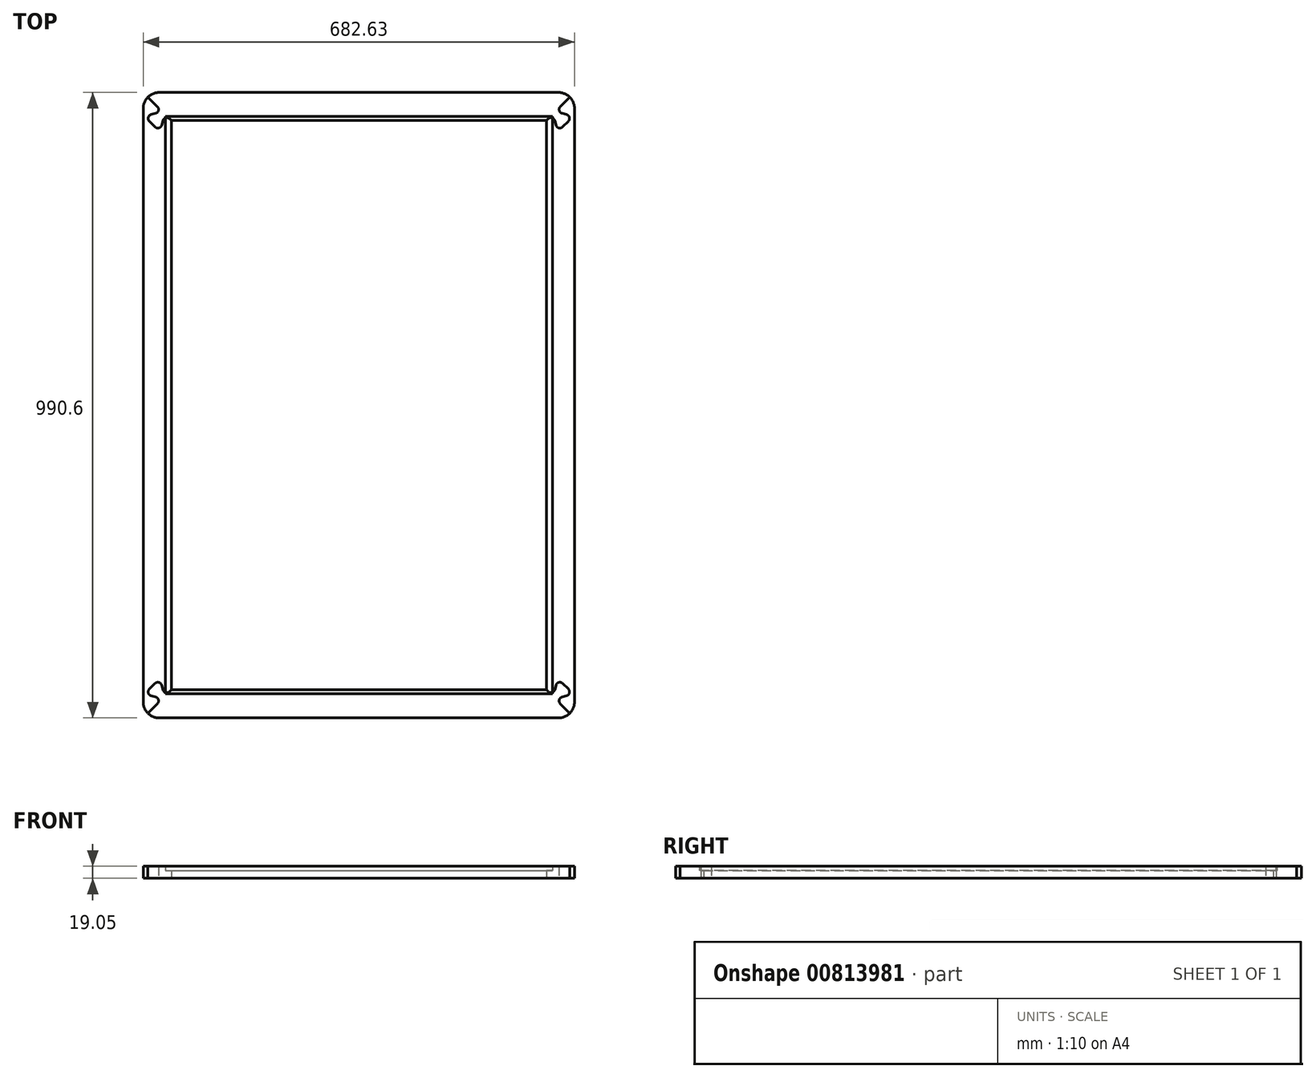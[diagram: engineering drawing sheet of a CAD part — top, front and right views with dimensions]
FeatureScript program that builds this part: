
annotation { "Feature Type Name" : "Feature", "Feature Type Description" : "" }
export const myFeature = defineFeature(function(context is Context, id is Id, definition is map)
    precondition{}
    {
        {
            var Q0;
            Q0=qCreatedBy(makeId("Top.planeOp"),FACE);
            var sketch = newSketch(context, id + "F0", { "sketchPlane" : qUnion([Q0])});
            skLineSegment(sketch, "E0.0", {"start": v(0, 0) * mm, "end": v(22.45, 22.45) * mm});
            skLineSegment(sketch, "E1", {"start": v(44.45, 44.45) * mm, "end": v(638.17, 44.45) * mm});
            skLineSegment(sketch, "E2", {"start": v(0, 0) * mm, "end": v(682.62, 0) * mm});
            skLineSegment(sketch, "E3", {"start": v(31.18, 44.65) * mm, "end": v(29.28, 51.73) * mm});
            skLineSegment(sketch, "E4.MirrorCS", {"start": v(19.6, 33.07) * mm, "end": v(12.52, 34.97) * mm});
            skLineSegment(sketch, "E5", {"start": v(9.67, 45.6) * mm, "end": v(18.66, 54.58) * mm});
            skArc(sketch, "E6.filletArc", {"start": v(29.28, 51.73) * mm, "mid": v(24.79, 56.22) * mm, "end": v(18.66, 54.58) * mm});
            skArc(sketch, "E7.filletArc", {"start": v(9.67, 45.6) * mm, "mid": v(8.03, 39.46) * mm, "end": v(12.52, 34.97) * mm});
            skArc(sketch, "E8.filletArc", {"start": v(22.45, 22.45) * mm, "mid": v(24.1, 28.58) * mm, "end": v(19.6, 33.07) * mm});
            skArc(sketch, "E9.filletArc", {"start": v(31.18, 44.65) * mm, "mid": v(35.66, 40.16) * mm, "end": v(41.8, 41.8) * mm});
            skLineSegment(sketch, "E10", {"start": v(41.8, 41.8) * mm, "end": v(44.45, 44.45) * mm});
            skLineSegment(sketch, "E11", {"start": v(341.31, 44.45) * mm, "end": v(341.31, 0) * mm, "construction": true});
            skPoint(sketch, "E11.endSnap0", {"position": v(341.31, 0) * mm});
            skLineSegment(sketch, "E12.MirrorCS", {"start": v(640.83, 41.8) * mm, "end": v(638.17, 44.45) * mm});
            skLineSegment(sketch, "E13.MirrorCS", {"start": v(651.45, 44.65) * mm, "end": v(653.35, 51.73) * mm});
            skArc(sketch, "E14.MirrorCS", {"start": v(651.45, 44.65) * mm, "mid": v(646.96, 40.16) * mm, "end": v(640.83, 41.8) * mm});
            skArc(sketch, "E15.MirrorCS", {"start": v(653.35, 51.73) * mm, "mid": v(657.84, 56.22) * mm, "end": v(663.97, 54.58) * mm});
            skLineSegment(sketch, "E16.MirrorCS", {"start": v(663.02, 33.07) * mm, "end": v(670.1, 34.97) * mm});
            skLineSegment(sketch, "E17.MirrorCS", {"start": v(672.95, 45.6) * mm, "end": v(663.97, 54.58) * mm});
            skArc(sketch, "E18.MirrorCS", {"start": v(660.17, 22.45) * mm, "mid": v(658.53, 28.58) * mm, "end": v(663.02, 33.07) * mm});
            skLineSegment(sketch, "E19.MirrorCS", {"start": v(682.62, 0) * mm, "end": v(660.17, 22.45) * mm});
            skArc(sketch, "E20.MirrorCS", {"start": v(672.95, 45.6) * mm, "mid": v(674.6, 39.46) * mm, "end": v(670.1, 34.97) * mm});
            skLineSegment(sketch, "E21", {"start": v(-140.17, 495.3) * mm, "end": v(823.27, 495.3) * mm, "construction": true});
            skArc(sketch, "E22.MirrorCS", {"start": v(31.18, 945.95) * mm, "mid": v(35.66, 950.44) * mm, "end": v(41.8, 948.8) * mm});
            skArc(sketch, "E23.MirrorCS", {"start": v(9.67, 945) * mm, "mid": v(8.03, 951.14) * mm, "end": v(12.52, 955.63) * mm});
            skLineSegment(sketch, "E24.MirrorCS", {"start": v(19.6, 957.53) * mm, "end": v(12.52, 955.63) * mm});
            skLineSegment(sketch, "E25.MirrorCS", {"start": v(31.18, 945.95) * mm, "end": v(29.28, 938.87) * mm});
            skLineSegment(sketch, "E26.MirrorCS", {"start": v(41.8, 948.8) * mm, "end": v(44.45, 946.15) * mm});
            skArc(sketch, "E27.MirrorCS", {"start": v(22.45, 968.15) * mm, "mid": v(24.1, 962.02) * mm, "end": v(19.6, 957.53) * mm});
            skLineSegment(sketch, "E28.MirrorCS", {"start": v(9.67, 945) * mm, "end": v(18.66, 936.02) * mm});
            skArc(sketch, "E29.MirrorCS", {"start": v(29.28, 938.87) * mm, "mid": v(24.79, 934.38) * mm, "end": v(18.66, 936.02) * mm});
            skArc(sketch, "E30.MirrorCS", {"start": v(651.45, 945.95) * mm, "mid": v(646.96, 950.44) * mm, "end": v(640.83, 948.8) * mm});
            skLineSegment(sketch, "E31.MirrorCS", {"start": v(640.83, 948.8) * mm, "end": v(638.17, 946.15) * mm});
            skLineSegment(sketch, "E32.MirrorCS", {"start": v(651.45, 945.95) * mm, "end": v(653.35, 938.87) * mm});
            skArc(sketch, "E33.MirrorCS", {"start": v(672.95, 945) * mm, "mid": v(674.6, 951.14) * mm, "end": v(670.1, 955.63) * mm});
            skLineSegment(sketch, "E34.MirrorCS", {"start": v(663.02, 957.53) * mm, "end": v(670.1, 955.63) * mm});
            skArc(sketch, "E35.MirrorCS", {"start": v(653.35, 938.87) * mm, "mid": v(657.84, 934.38) * mm, "end": v(663.97, 936.02) * mm});
            skLineSegment(sketch, "E36.MirrorCS", {"start": v(672.95, 945) * mm, "end": v(663.97, 936.02) * mm});
            skArc(sketch, "E37.MirrorCS", {"start": v(660.17, 968.15) * mm, "mid": v(658.53, 962.02) * mm, "end": v(663.02, 957.53) * mm});
            skLineSegment(sketch, "E38.MirrorCS", {"start": v(0, 990.6) * mm, "end": v(22.45, 968.15) * mm});
            skLineSegment(sketch, "E39.MirrorCS", {"start": v(341.31, 946.15) * mm, "end": v(341.31, 990.6) * mm, "construction": true});
            skPoint(sketch, "E40.MirrorP", {"position": v(341.31, 990.6) * mm});
            skLineSegment(sketch, "E41.MirrorCS", {"start": v(0, 990.6) * mm, "end": v(682.62, 990.6) * mm});
            skLineSegment(sketch, "E42.MirrorCS", {"start": v(682.62, 990.6) * mm, "end": v(660.17, 968.15) * mm});
            skLineSegment(sketch, "E43.MirrorCS", {"start": v(44.45, 946.15) * mm, "end": v(638.17, 946.15) * mm});
            skSolve(sketch);
        }
        {
            var Q0;
            Q0 = qSketchRegion(id + "F0", true);
            extrude(context, id + "F1", {"entities" : qUnion([Q0]), "depth" : 19.05 * mm, "offsetDistance" : 25.4 * mm});
        }
        {
            var Q0;
            Q0=qCreatedBy(makeId("Top.planeOp"),FACE);
            var sketch = newSketch(context, id + "F2", { "sketchPlane" : qUnion([Q0])});
            skLineSegment(sketch, "E44.left", {"start": v(0, 0) * mm, "end": v(0, 990.6) * mm});
            skLineSegment(sketch, "E44.right", {"start": v(44.45, 44.45) * mm, "end": v(44.45, 946.15) * mm});
            skLineSegment(sketch, "E45.0", {"start": v(9.67, 45.6) * mm, "end": v(18.66, 54.58) * mm});
            skArc(sketch, "E45.1", {"start": v(9.67, 45.6) * mm, "mid": v(8.03, 39.46) * mm, "end": v(12.52, 34.97) * mm});
            skLineSegment(sketch, "E45.2", {"start": v(19.6, 33.07) * mm, "end": v(12.52, 34.97) * mm});
            skArc(sketch, "E45.3", {"start": v(22.45, 22.45) * mm, "mid": v(24.1, 28.58) * mm, "end": v(19.6, 33.07) * mm});
            skArc(sketch, "E45.4", {"start": v(29.28, 51.73) * mm, "mid": v(24.79, 56.22) * mm, "end": v(18.66, 54.58) * mm});
            skLineSegment(sketch, "E45.5", {"start": v(31.18, 44.65) * mm, "end": v(29.28, 51.73) * mm});
            skArc(sketch, "E45.6", {"start": v(31.18, 44.65) * mm, "mid": v(35.66, 40.16) * mm, "end": v(41.8, 41.8) * mm});
            skLineSegment(sketch, "E46", {"start": v(0, 0) * mm, "end": v(22.45, 22.45) * mm});
            skLineSegment(sketch, "E47", {"start": v(41.8, 41.8) * mm, "end": v(44.45, 44.45) * mm});
            skLineSegment(sketch, "E48", {"start": v(44.45, 495.3) * mm, "end": v(0, 495.3) * mm, "construction": true});
            skLineSegment(sketch, "E49.MirrorCS", {"start": v(41.8, 948.8) * mm, "end": v(44.45, 946.15) * mm});
            skArc(sketch, "E50.MirrorCS", {"start": v(31.18, 945.95) * mm, "mid": v(35.66, 950.44) * mm, "end": v(41.8, 948.8) * mm});
            skLineSegment(sketch, "E51.MirrorCS", {"start": v(31.18, 945.95) * mm, "end": v(29.28, 938.87) * mm});
            skArc(sketch, "E52.MirrorCS", {"start": v(29.28, 938.87) * mm, "mid": v(24.79, 934.38) * mm, "end": v(18.66, 936.02) * mm});
            skLineSegment(sketch, "E53.MirrorCS", {"start": v(19.6, 957.53) * mm, "end": v(12.52, 955.63) * mm});
            skLineSegment(sketch, "E54.MirrorCS", {"start": v(9.67, 945) * mm, "end": v(18.66, 936.02) * mm});
            skArc(sketch, "E55.MirrorCS", {"start": v(9.67, 945) * mm, "mid": v(8.03, 951.14) * mm, "end": v(12.52, 955.63) * mm});
            skArc(sketch, "E56.MirrorCS", {"start": v(22.45, 968.15) * mm, "mid": v(24.1, 962.02) * mm, "end": v(19.6, 957.53) * mm});
            skLineSegment(sketch, "E57.MirrorCS", {"start": v(0, 990.6) * mm, "end": v(22.45, 968.15) * mm});
            skLineSegment(sketch, "E58.0", {"start": v(44.45, 44.45) * mm, "end": v(638.17, 44.45) * mm, "construction": true});
            skLineSegment(sketch, "E59", {"start": v(341.31, 44.45) * mm, "end": v(341.31, 1108) * mm, "construction": true});
            skLineSegment(sketch, "E60.MirrorCS", {"start": v(0, 990.6) * mm, "end": v(0, 0) * mm});
            skLineSegment(sketch, "E61.MirrorCS", {"start": v(44.45, 946.15) * mm, "end": v(44.45, 44.45) * mm});
            skLineSegment(sketch, "E62.MirrorCS", {"start": v(341.31, 946.15) * mm, "end": v(341.31, -117.4) * mm, "construction": true});
            skLineSegment(sketch, "E63.MirrorCS", {"start": v(638.18, 495.3) * mm, "end": v(682.62, 495.3) * mm, "construction": true});
            skLineSegment(sketch, "E64.MirrorCS", {"start": v(651.45, 945.95) * mm, "end": v(653.35, 938.87) * mm});
            skArc(sketch, "E65.MirrorCS", {"start": v(651.45, 945.95) * mm, "mid": v(646.96, 950.44) * mm, "end": v(640.83, 948.8) * mm});
            skLineSegment(sketch, "E66.MirrorCS", {"start": v(640.83, 948.8) * mm, "end": v(638.18, 946.15) * mm});
            skLineSegment(sketch, "E67.MirrorCS", {"start": v(651.45, 44.65) * mm, "end": v(653.35, 51.73) * mm});
            skArc(sketch, "E68.MirrorCS", {"start": v(651.45, 44.65) * mm, "mid": v(646.96, 40.16) * mm, "end": v(640.83, 41.8) * mm});
            skLineSegment(sketch, "E69.MirrorCS", {"start": v(640.83, 41.8) * mm, "end": v(638.18, 44.45) * mm});
            skArc(sketch, "E70.MirrorCS", {"start": v(660.17, 22.45) * mm, "mid": v(658.53, 28.58) * mm, "end": v(663.02, 33.07) * mm});
            skLineSegment(sketch, "E71.MirrorCS", {"start": v(663.02, 33.07) * mm, "end": v(670.1, 34.97) * mm});
            skArc(sketch, "E72.MirrorCS", {"start": v(653.35, 938.87) * mm, "mid": v(657.84, 934.38) * mm, "end": v(663.97, 936.02) * mm});
            skArc(sketch, "E73.MirrorCS", {"start": v(653.35, 51.73) * mm, "mid": v(657.84, 56.22) * mm, "end": v(663.97, 54.58) * mm});
            skArc(sketch, "E74.MirrorCS", {"start": v(660.17, 968.15) * mm, "mid": v(658.53, 962.02) * mm, "end": v(663.02, 957.53) * mm});
            skArc(sketch, "E75.MirrorCS", {"start": v(672.95, 45.6) * mm, "mid": v(674.6, 39.46) * mm, "end": v(670.1, 34.97) * mm});
            skLineSegment(sketch, "E76.MirrorCS", {"start": v(672.95, 945) * mm, "end": v(663.97, 936.02) * mm});
            skLineSegment(sketch, "E77.MirrorCS", {"start": v(663.02, 957.53) * mm, "end": v(670.1, 955.63) * mm});
            skArc(sketch, "E78.MirrorCS", {"start": v(672.95, 945) * mm, "mid": v(674.6, 951.14) * mm, "end": v(670.1, 955.63) * mm});
            skLineSegment(sketch, "E79.MirrorCS", {"start": v(672.95, 45.6) * mm, "end": v(663.97, 54.58) * mm});
            skLineSegment(sketch, "E80.MirrorCS", {"start": v(682.62, 990.6) * mm, "end": v(660.17, 968.15) * mm});
            skLineSegment(sketch, "E81.MirrorCS", {"start": v(682.62, 0) * mm, "end": v(660.17, 22.45) * mm});
            skLineSegment(sketch, "E82.MirrorCS", {"start": v(682.62, 0) * mm, "end": v(682.62, 990.6) * mm});
            skLineSegment(sketch, "E83.MirrorCS", {"start": v(638.18, 44.45) * mm, "end": v(638.18, 946.15) * mm});
            skLineSegment(sketch, "E84.MirrorCS", {"start": v(638.18, 946.15) * mm, "end": v(638.18, 44.45) * mm});
            skLineSegment(sketch, "E85.MirrorCS", {"start": v(682.62, 990.6) * mm, "end": v(682.62, 0) * mm});
            skSolve(sketch);
        }
        {
            var Q0;
            Q0 = qSketchRegion(id + "F2", true);
            extrude(context, id + "F3", {"entities" : qUnion([Q0]), "depth" : 19.05 * mm, "offsetDistance" : 25.4 * mm});
        }
        {
            var Q0;
            Q0=makeQuery(id+"F3.opExtrude","CAP_FACE",FACE,{"disambiguationData":[OSD([sQuery(id+"F2.wireOp",EDGE,"E51.MirrorCS"),sQuery(id+"F2.wireOp",EDGE,"E49.MirrorCS"),sQuery(id+"F2.wireOp",EDGE,"E50.MirrorCS"),sQuery(id+"F2.wireOp",EDGE,"E45.6"),sQuery(id+"F2.wireOp",EDGE,"E45.5"),sQuery(id+"F2.wireOp",EDGE,"E47"),sQuery(id+"F2.wireOp",EDGE,"E45.0"),sQuery(id+"F2.wireOp",EDGE,"E45.2"),sQuery(id+"F2.wireOp",EDGE,"E45.1"),sQuery(id+"F2.wireOp",EDGE,"E53.MirrorCS"),sQuery(id+"F2.wireOp",EDGE,"E56.MirrorCS"),sQuery(id+"F2.wireOp",EDGE,"E52.MirrorCS"),sQuery(id+"F2.wireOp",EDGE,"E54.MirrorCS"),sQuery(id+"F2.wireOp",EDGE,"E45.4"),sQuery(id+"F2.wireOp",EDGE,"E45.3"),sQuery(id+"F2.wireOp",EDGE,"E55.MirrorCS"),sQuery(id+"F2.wireOp",EDGE,"E46"),sQuery(id+"F2.wireOp",EDGE,"E57.MirrorCS"),sQuery(id+"F2.wireOp",EDGE,"E44.right"),sQuery(id+"F2.wireOp",EDGE,"E44.left")])],"isStart":false});
            var sketch = newSketch(context, id + "F4", { "sketchPlane" : qUnion([Q0])});
            skLineSegment(sketch, "E86.bottom", {"start": v(34.92, 952.5) * mm, "end": v(647.7, 952.5) * mm});
            skLineSegment(sketch, "E86.top", {"start": v(34.93, 38.1) * mm, "end": v(647.7, 38.1) * mm});
            skLineSegment(sketch, "E86.left", {"start": v(34.92, 952.5) * mm, "end": v(34.93, 38.1) * mm});
            skLineSegment(sketch, "E86.right", {"start": v(647.7, 952.5) * mm, "end": v(647.7, 38.1) * mm});
            skSolve(sketch);
        }
        {
            var Q0;
            Q0 = qSketchRegion(id + "F4", true);
            extrude(context, id + "F5", {"entities" : qUnion([Q0]), "operationType" : NewBodyOperationType.REMOVE, "oppositeDirection" : true, "depth" : 6.73 * mm, "offsetDistance" : 25.4 * mm});
        }
        {
            var Q0;
            Q0=makeQuery(id+"F1.opExtrude","CAP_FACE",FACE,{"disambiguationData":[OSD([sQuery(id+"F0.wireOp",EDGE,"E0.0"),sQuery(id+"F0.wireOp",EDGE,"E1"),sQuery(id+"F0.wireOp",EDGE,"E2"),sQuery(id+"F0.wireOp",EDGE,"E3"),sQuery(id+"F0.wireOp",EDGE,"E4.MirrorCS"),sQuery(id+"F0.wireOp",EDGE,"E5"),sQuery(id+"F0.wireOp",EDGE,"E6.filletArc"),sQuery(id+"F0.wireOp",EDGE,"E7.filletArc"),sQuery(id+"F0.wireOp",EDGE,"E8.filletArc"),sQuery(id+"F0.wireOp",EDGE,"E9.filletArc"),sQuery(id+"F0.wireOp",EDGE,"E10"),sQuery(id+"F0.wireOp",EDGE,"E12.MirrorCS"),sQuery(id+"F0.wireOp",EDGE,"E13.MirrorCS"),sQuery(id+"F0.wireOp",EDGE,"E14.MirrorCS"),sQuery(id+"F0.wireOp",EDGE,"E15.MirrorCS"),sQuery(id+"F0.wireOp",EDGE,"E16.MirrorCS"),sQuery(id+"F0.wireOp",EDGE,"E17.MirrorCS"),sQuery(id+"F0.wireOp",EDGE,"E18.MirrorCS"),sQuery(id+"F0.wireOp",EDGE,"E19.MirrorCS"),sQuery(id+"F0.wireOp",EDGE,"E20.MirrorCS")])],"isStart":false});
            var sketch = newSketch(context, id + "F6", { "sketchPlane" : qUnion([Q0])});
            skLineSegment(sketch, "E87.0", {"start": v(0, 25.4) * mm, "end": v(0, 965.2) * mm});
            skLineSegment(sketch, "E88.0", {"start": v(25.4, 990.6) * mm, "end": v(657.23, 990.6) * mm});
            skLineSegment(sketch, "E89.0", {"start": v(682.62, 965.2) * mm, "end": v(682.62, 25.4) * mm});
            skLineSegment(sketch, "E90.0", {"start": v(25.4, 0) * mm, "end": v(657.22, 0) * mm});
            skLineSegment(sketch, "E91.bottom", {"start": v(-257.05, 1207.8) * mm, "end": v(900.49, 1207.8) * mm});
            skLineSegment(sketch, "E91.top", {"start": v(-257.05, -217.24) * mm, "end": v(900.49, -217.24) * mm});
            skLineSegment(sketch, "E91.left", {"start": v(-257.05, 1207.8) * mm, "end": v(-257.05, -217.24) * mm});
            skLineSegment(sketch, "E91.right", {"start": v(900.49, 1207.8) * mm, "end": v(900.49, -217.24) * mm});
            skPoint(sketch, "E92.visualSharp", {"position": v(0, 990.6) * mm});
            skArc(sketch, "E92.filletArc", {"start": v(25.4, 990.6) * mm, "mid": v(7.44, 983.16) * mm, "end": v(0, 965.2) * mm});
            skPoint(sketch, "E93.visualSharp", {"position": v(682.62, 990.6) * mm});
            skArc(sketch, "E93.filletArc", {"start": v(682.62, 965.2) * mm, "mid": v(675.19, 983.16) * mm, "end": v(657.23, 990.6) * mm});
            skPoint(sketch, "E94.visualSharp", {"position": v(0, 0) * mm});
            skArc(sketch, "E94.filletArc", {"start": v(0, 25.4) * mm, "mid": v(7.44, 7.44) * mm, "end": v(25.4, 0) * mm});
            skPoint(sketch, "E95.visualSharp", {"position": v(682.62, 0) * mm});
            skArc(sketch, "E95.filletArc", {"start": v(657.22, 0) * mm, "mid": v(675.19, 7.44) * mm, "end": v(682.62, 25.4) * mm});
            skSolve(sketch);
        }
        {
            var Q0;
            Q0 = qSketchRegion(id + "F6", true);
            extrude(context, id + "F7", {"entities" : qUnion([Q0]), "operationType" : NewBodyOperationType.REMOVE, "oppositeDirection" : true, "depth" : 25.4 * mm, "offsetDistance" : 25.4 * mm});
        }
    });
